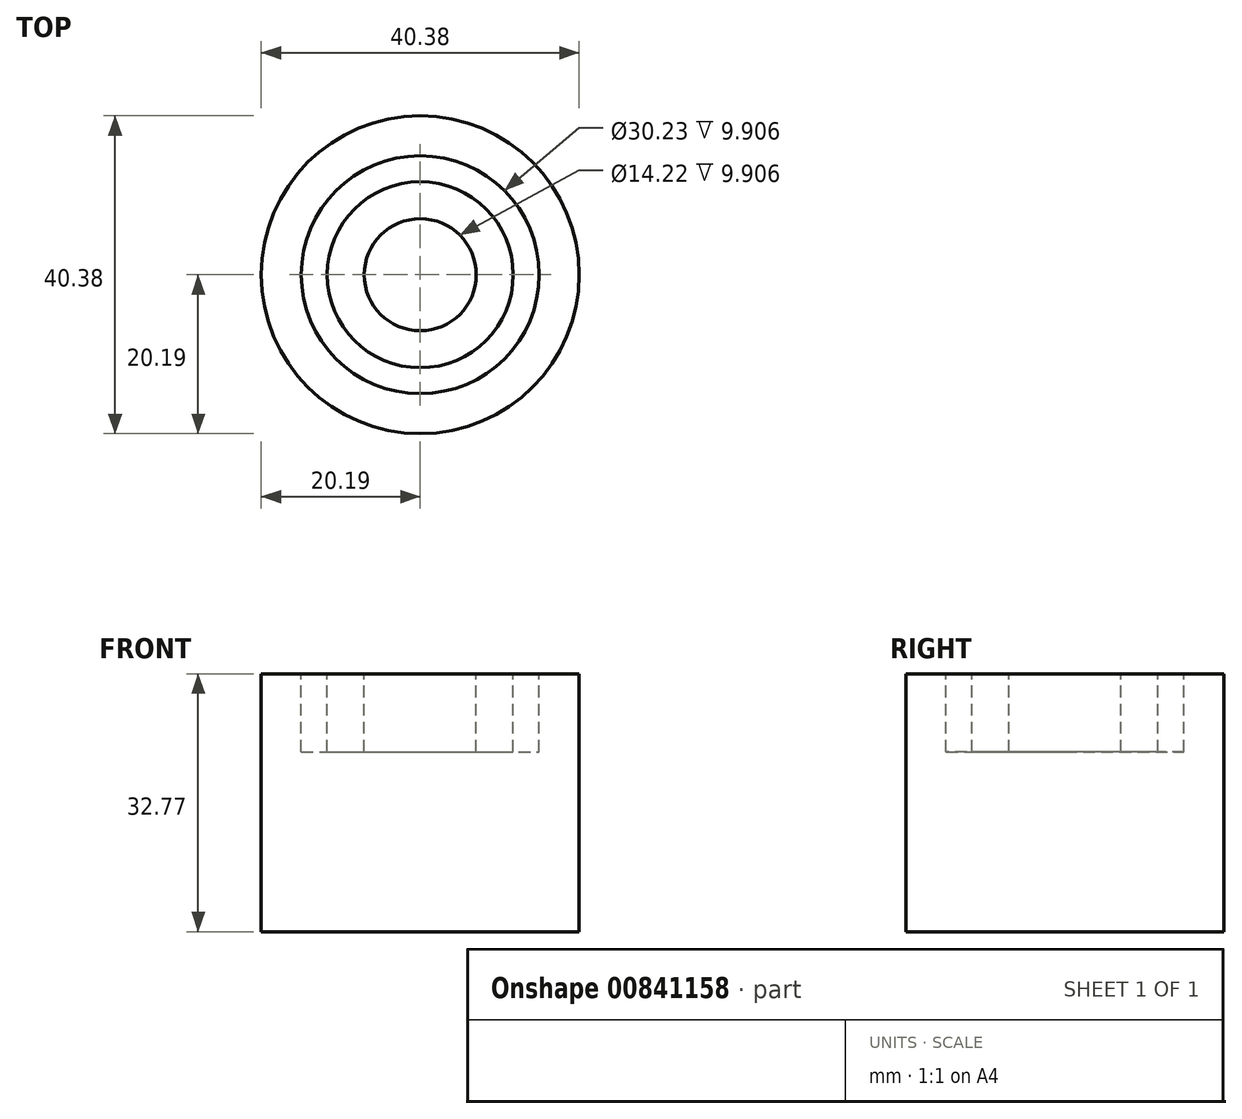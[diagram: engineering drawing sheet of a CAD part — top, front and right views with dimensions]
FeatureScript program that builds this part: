
annotation { "Feature Type Name" : "Feature", "Feature Type Description" : "" }
export const myFeature = defineFeature(function(context is Context, id is Id, definition is map)
    precondition{}
    {
        {
            var Q0;
            Q0=qCreatedBy(makeId("Top.planeOp"),FACE);
            var sketch = newSketch(context, id + "F0", { "sketchPlane" : qUnion([Q0])});
            skCircle(sketch, "E0", {"center": v(0, 0) * mm, "radius": 15.11 * mm});
            skCircle(sketch, "E1.0", {"center": v(0, 0) * mm, "radius": 11.81 * mm});
            skCircle(sketch, "E2.0", {"center": v(0, 0) * mm, "radius": 20.2 * mm});
            skCircle(sketch, "E3", {"center": v(0, 0) * mm, "radius": 7.11 * mm});
            skSolve(sketch);
        }
        {
            var Q0;
            Q0 = qSketchRegion(id + "F0", true);
            var Q1;
            Q1=makeQuery(id+"F0.imprint","IMPRINT",FACE,{"disambiguationData":[TD([[makeQuery(id+"F0.imprint","IMPRINT",EDGE,{"derivedFrom":sQuery(id+"F0.wireOp",EDGE,"E1.0")}),1.0]])]});
            extrude(context, id + "F1", {"entities" : qUnion([Q0, Q1]), "depth" : 9.9 * mm, "offsetDistance" : 25.4 * mm});
        }
        {
            var Q0;
            Q0=makeQuery(id+"F1.opExtrude","CAP_FACE",FACE,{"disambiguationData":[OSD([sQuery(id+"F0.wireOp",EDGE,"E0"),sQuery(id+"F0.wireOp",EDGE,"E2.0")])],"isStart":false});
            var sketch = newSketch(context, id + "F2", { "sketchPlane" : qUnion([Q0])});
            skCircle(sketch, "E4", {"center": v(0, 0) * mm, "radius": 20.2 * mm});
            skSolve(sketch);
        }
        {
            var Q0;
            Q0 = qSketchRegion(id + "F2", true);
            extrude(context, id + "F3", {"entities" : qUnion([Q0]), "operationType" : NewBodyOperationType.ADD, "depth" : 22.86 * mm, "offsetDistance" : 25.4 * mm});
        }
        {
            var Q0;
            Q0=qCreatedBy(makeId("Top.planeOp"),FACE);
            var sketch = newSketch(context, id + "F4", { "sketchPlane" : qUnion([Q0])});
            skLineSegment(sketch, "E5", {"start": v(0, 74.99) * mm, "end": v(0, -48.67) * mm});
            skSolve(sketch);
        }
        {
            var Q0;
            Q0=makeQuery(id+"F1.opExtrude","SWEPT_BODY",BODY,{"disambiguationData":[OSD([sQuery(id+"F0.wireOp",EDGE,"E0"),sQuery(id+"F0.wireOp",EDGE,"E2.0")])]});
            var Q1;
            Q1=makeQuery(id+"F1.opExtrude","SWEPT_BODY",BODY,{"disambiguationData":[OSD([sQuery(id+"F0.wireOp",EDGE,"E1.0"),sQuery(id+"F0.wireOp",EDGE,"E3")])]});
            var Q2;
            Q2=sQuery(id+"F4.wireOp",EDGE,"E5");
            transform(context, id + "F5", {"entities" : qUnion([Q0, Q1]), "transformType" : TransformType.ROTATION, "transformAxis" : qUnion([Q2]), "angle" : 180 * degree, "makeCopy" : false});
        }
    });
